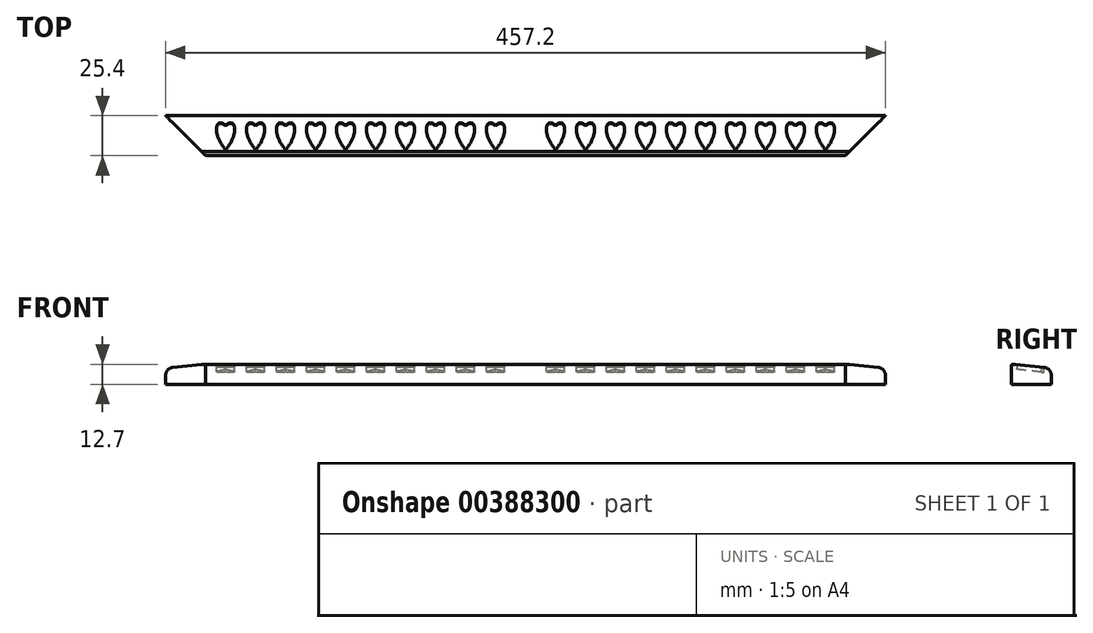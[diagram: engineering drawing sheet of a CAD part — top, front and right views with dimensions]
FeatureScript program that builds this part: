
annotation { "Feature Type Name" : "Feature", "Feature Type Description" : "" }
export const myFeature = defineFeature(function(context is Context, id is Id, definition is map)
    precondition{}
    {
        {
            var Q0;
            Q0=qCreatedBy(makeId("Top.planeOp"),FACE);
            var sketch = newSketch(context, id + "F0", { "sketchPlane" : qUnion([Q0])});
            skLineSegment(sketch, "E0.bottom", {"start": v(-228.6, 12.7) * mm, "end": v(228.6, 12.7) * mm});
            skLineSegment(sketch, "E0.top", {"start": v(-228.6, -12.7) * mm, "end": v(228.6, -12.7) * mm});
            skLineSegment(sketch, "E0.left", {"start": v(-228.6, 12.7) * mm, "end": v(-228.6, -12.7) * mm});
            skLineSegment(sketch, "E0.right", {"start": v(228.6, 12.7) * mm, "end": v(228.6, -12.7) * mm});
            skPoint(sketch, "E0.middle", {"position": v(0, 0) * mm});
            skLineSegment(sketch, "E1", {"start": v(-228.6, 12.7) * mm, "end": v(-203.2, -12.7) * mm});
            skLineSegment(sketch, "E2.MirrorCS", {"start": v(228.6, 12.7) * mm, "end": v(203.2, -12.7) * mm});
            skSolve(sketch);
        }
        {
            var Q0;
            Q0=makeQuery(id+"F0.imprint","IMPRINT",FACE,{"disambiguationData":[TD([[makeQuery(id+"F0.imprint","IMPRINT",EDGE,{"derivedFrom":sQuery(id+"F0.wireOp",EDGE,"E0.bottom")}),-1.0]])]});
            extrude(context, id + "F1", {"entities" : qUnion([Q0]), "depth" : 12.7 * mm});
        }
        {
            var Q0;
            Q0=makeQuery(id+"F1.opExtrude","CAP_EDGE",EDGE,{"disambiguationData":[OSD([sQuery(id+"F0.wireOp",EDGE,"E0.bottom")])],"isStart":false});
            chamfer(context, id + "F2", {"entities" : qUnion([Q0]), "chamferType" : ChamferType.TWO_OFFSETS, "width1" : 2.54 * mm, "oppositeDirection" : false, "width2" : 22.86 * mm, "tangentPropagation" : true});
        }
        {
            var Q0;
            {var subQ0=sQuery(id+"F0.wireOp",EDGE,"E0.bottom");Q0=makeQuery(id+"F2.opChamfer","BLEND_EDGE",EDGE,{"blendedFrom":[makeQuery(id+"F1.opExtrude","CAP_EDGE",EDGE,{"disambiguationData":[OSD([subQ0])],"isStart":false}),makeQuery(id+"F1.opExtrude","SWEPT_FACE",FACE,{"disambiguationData":[OSD([subQ0])]})],"blendedInto":[makeQuery(id+"F1.opExtrude","SWEPT_FACE",FACE,{"disambiguationData":[OSD([subQ0])]})]});}
            fillet(context, id + "F3", {"entities" : qUnion([Q0]), "radius" : 5.08 * mm, "tangentPropagation" : true, "allowEdgeOverflow" : false});
        }
        {
            var Q0;
            Q0=makeQuery(id+"F2.opChamfer","BLEND_FACE",FACE,{"disambiguationData":[OSD([sQuery(id+"F0.wireOp",EDGE,"E0.bottom")])]});
            var sketch = newSketch(context, id + "F4", { "sketchPlane" : qUnion([Q0])});
            skLineSegment(sketch, "E3.bottom", {"start": v(-6.1, 6.86) * mm, "end": v(6.1, 6.86) * mm});
            skLineSegment(sketch, "E3.top", {"start": v(-6.1, -11.6) * mm, "end": v(6.1, -11.6) * mm});
            skLineSegment(sketch, "E3.left", {"start": v(-6.1, 6.86) * mm, "end": v(-6.1, -11.6) * mm});
            skLineSegment(sketch, "E3.right", {"start": v(6.1, 6.86) * mm, "end": v(6.1, -11.6) * mm});
            skPoint(sketch, "E3.middle", {"position": v(0, -2.36) * mm});
            skPoint(sketch, "E3.middle.positionSnap0", {"position": v(-189.51, -2.36) * mm});
            skPoint(sketch, "E3.centerSnap0", {"position": v(-189.51, -2.36) * mm});
            skEllipticalArc(sketch, "E4", {});
            skEllipticalArc(sketch, "E5", {});
            skEllipticalArc(sketch, "E6.0.1.0", {});
            skEllipticalArc(sketch, "E6.0.1.1", {});
            skEllipticalArc(sketch, "E6.1.0.0", {});
            skEllipticalArc(sketch, "E6.1.0.1", {});
            skEllipticalArc(sketch, "E6.1.1.0", {});
            skEllipticalArc(sketch, "E6.1.1.1", {});
            skEllipticalArc(sketch, "E6.2.0.0", {});
            skEllipticalArc(sketch, "E6.2.0.1", {});
            skEllipticalArc(sketch, "E6.2.1.0", {});
            skEllipticalArc(sketch, "E6.2.1.1", {});
            skEllipticalArc(sketch, "E6.3.0.0", {});
            skEllipticalArc(sketch, "E6.3.0.1", {});
            skEllipticalArc(sketch, "E6.3.1.0", {});
            skEllipticalArc(sketch, "E6.3.1.1", {});
            skEllipticalArc(sketch, "E6.4.0.0", {});
            skEllipticalArc(sketch, "E6.4.0.1", {});
            skEllipticalArc(sketch, "E6.4.1.0", {});
            skEllipticalArc(sketch, "E6.4.1.1", {});
            skEllipticalArc(sketch, "E6.5.0.0", {});
            skEllipticalArc(sketch, "E6.5.0.1", {});
            skEllipticalArc(sketch, "E6.5.1.0", {});
            skEllipticalArc(sketch, "E6.5.1.1", {});
            skEllipticalArc(sketch, "E6.6.0.0", {});
            skEllipticalArc(sketch, "E6.6.0.1", {});
            skEllipticalArc(sketch, "E6.6.1.0", {});
            skEllipticalArc(sketch, "E6.6.1.1", {});
            skEllipticalArc(sketch, "E6.7.0.0", {});
            skEllipticalArc(sketch, "E6.7.0.1", {});
            skEllipticalArc(sketch, "E6.7.1.0", {});
            skEllipticalArc(sketch, "E6.7.1.1", {});
            skEllipticalArc(sketch, "E6.8.0.0", {});
            skEllipticalArc(sketch, "E6.8.0.1", {});
            skEllipticalArc(sketch, "E6.8.1.0", {});
            skEllipticalArc(sketch, "E6.8.1.1", {});
            skEllipticalArc(sketch, "E6.9.0.0", {});
            skEllipticalArc(sketch, "E6.9.0.1", {});
            skEllipticalArc(sketch, "E6.9.1.0", {});
            skEllipticalArc(sketch, "E6.9.1.1", {});
            skLineSegment(sketch, "E6.direction1", {"start": v(0, -10.06) * mm, "end": v(19.05, -10.06) * mm, "construction": true});
            skLineSegment(sketch, "E6.direction2", {"start": v(0, -10.06) * mm, "end": v(-190.5, -10.06) * mm, "construction": true});
            skEllipticalArc(sketch, "E7.0.10.0", {});
            skEllipticalArc(sketch, "E7.4.10.0", {});
            skEllipticalArc(sketch, "E7.0.10.1", {});
            skEllipticalArc(sketch, "E7.4.10.1", {});
            const initialGuessF4  = {"E4": [0, -0.0023644506516210797, 0.41355218363854207, 0.9104804179156154, 0.010033, 0.004445, 3.9394450816196147, 0.7978524280298204], "E5": [0, -0.0023644506516210797, -0.41355218363854224, 0.9104804179156154, 0.010033, 0.004445, 5.485332879149764, 2.3437402255599724], "E6.0.1.0": [-0.1905, -0.0023644506516211005, -0.4135521836385429, 0.9104804179156151, 0.010033, 0.004445, 5.485332879149764, 2.34374022555997], "E6.0.1.1": [-0.1905, -0.0023644506516211005, 0.4135521836385428, 0.9104804179156151, 0.010033, 0.004445, 3.939445081619611, 0.797852428029822], "E6.1.0.0": [0.01905, -0.0023644506516210797, -0.41355218363854224, 0.9104804179156153, 0.010033, 0.004445, 5.485332879149765, 2.3437402255599733], "E6.1.0.1": [0.01905, -0.0023644506516210797, 0.41355218363854207, 0.9104804179156155, 0.010033, 0.004445, 3.939445081619616, 0.7978524280298207], "E6.1.1.0": [-0.17145, -0.0023644506516211005, -0.41355218363854285, 0.9104804179156151, 0.010033, 0.004445, 5.485332879149765, 2.343740225559971], "E6.1.1.1": [-0.17145, -0.0023644506516211005, 0.4135521836385428, 0.9104804179156152, 0.010033, 0.004445, 3.9394450816196143, 0.7978524280298254], "E6.2.0.0": [0.0381, -0.0023644506516210797, -0.41355218363854224, 0.9104804179156153, 0.010033, 0.004445, 5.485332879149765, 2.3437402255599724], "E6.2.0.1": [0.0381, -0.0023644506516210797, 0.41355218363854207, 0.9104804179156155, 0.010033, 0.004445, 3.939445081619614, 0.7978524280298207], "E6.2.1.0": [-0.1524, -0.0023644506516211005, -0.41355218363854285, 0.9104804179156151, 0.010033, 0.004445, 5.485332879149764, 2.343740225559971], "E6.2.1.1": [-0.1524, -0.0023644506516211005, 0.4135521836385428, 0.9104804179156152, 0.010033, 0.004445, 3.9394450816196143, 0.7978524280298218], "E6.3.0.0": [0.05715, -0.0023644506516210797, -0.41355218363854224, 0.9104804179156153, 0.010033, 0.004445, 5.485332879149765, 2.3437402255599724], "E6.3.0.1": [0.05715, -0.0023644506516210797, 0.41355218363854207, 0.9104804179156155, 0.010033, 0.004445, 3.939445081619614, 0.7978524280298207], "E6.3.1.0": [-0.13335, -0.0023644506516211005, -0.41355218363854285, 0.9104804179156151, 0.010033, 0.004445, 5.485332879149764, 2.343740225559971], "E6.3.1.1": [-0.13335, -0.0023644506516211005, 0.4135521836385428, 0.9104804179156152, 0.010033, 0.004445, 3.9394450816196143, 0.7978524280298218], "E6.4.0.0": [0.0762, -0.0023644506516210797, -0.41355218363854224, 0.9104804179156153, 0.010033, 0.004445, 5.485332879149765, 2.3437402255599724], "E6.4.0.1": [0.0762, -0.0023644506516210797, 0.41355218363854207, 0.9104804179156155, 0.010033, 0.004445, 3.939445081619614, 0.7978524280298207], "E6.4.1.0": [-0.1143, -0.0023644506516211005, -0.41355218363854285, 0.9104804179156151, 0.010033, 0.004445, 5.485332879149764, 2.343740225559971], "E6.4.1.1": [-0.1143, -0.0023644506516211005, 0.4135521836385428, 0.9104804179156152, 0.010033, 0.004445, 3.9394450816196143, 0.7978524280298218], "E6.5.0.0": [0.09525, -0.0023644506516210797, -0.41355218363854224, 0.9104804179156153, 0.010033, 0.004445, 5.485332879149765, 2.3437402255599724], "E6.5.0.1": [0.09525, -0.0023644506516210797, 0.41355218363854207, 0.9104804179156155, 0.010033, 0.004445, 3.939445081619614, 0.7978524280298207], "E6.5.1.0": [-0.09525, -0.0023644506516211005, -0.41355218363854285, 0.9104804179156151, 0.010033, 0.004445, 5.485332879149764, 2.343740225559971], "E6.5.1.1": [-0.09525, -0.0023644506516211005, 0.4135521836385428, 0.9104804179156152, 0.010033, 0.004445, 3.9394450816196143, 0.7978524280298218], "E6.6.0.0": [0.1143, -0.0023644506516210797, -0.41355218363854224, 0.9104804179156153, 0.010033, 0.004445, 5.485332879149765, 2.3437402255599724], "E6.6.0.1": [0.1143, -0.0023644506516210797, 0.41355218363854207, 0.9104804179156155, 0.010033, 0.004445, 3.939445081619614, 0.7978524280298207], "E6.6.1.0": [-0.0762, -0.0023644506516211005, -0.41355218363854285, 0.9104804179156151, 0.010033, 0.004445, 5.485332879149764, 2.343740225559971], "E6.6.1.1": [-0.0762, -0.0023644506516211005, 0.4135521836385428, 0.9104804179156152, 0.010033, 0.004445, 3.9394450816196143, 0.7978524280298218], "E6.7.0.0": [0.13335, -0.0023644506516210797, -0.41355218363854224, 0.9104804179156153, 0.010033, 0.004445, 5.485332879149765, 2.3437402255599724], "E6.7.0.1": [0.13335, -0.0023644506516210797, 0.41355218363854207, 0.9104804179156155, 0.010033, 0.004445, 3.939445081619614, 0.7978524280298207], "E6.7.1.0": [-0.05715, -0.0023644506516211005, -0.41355218363854285, 0.9104804179156151, 0.010033, 0.004445, 5.485332879149764, 2.343740225559971], "E6.7.1.1": [-0.05715, -0.0023644506516211005, 0.4135521836385428, 0.9104804179156152, 0.010033, 0.004445, 3.9394450816196143, 0.7978524280298218], "E6.8.0.0": [0.1524, -0.0023644506516210797, -0.41355218363854224, 0.9104804179156153, 0.010033, 0.004445, 5.485332879149765, 2.3437402255599724], "E6.8.0.1": [0.1524, -0.0023644506516210797, 0.41355218363854207, 0.9104804179156155, 0.010033, 0.004445, 3.939445081619614, 0.7978524280298207], "E6.8.1.0": [-0.0381, -0.0023644506516211005, -0.41355218363854285, 0.9104804179156151, 0.010033, 0.004445, 5.485332879149764, 2.343740225559971], "E6.8.1.1": [-0.0381, -0.0023644506516211005, 0.4135521836385428, 0.9104804179156152, 0.010033, 0.004445, 3.9394450816196143, 0.7978524280298218], "E6.9.0.0": [0.17145, -0.0023644506516210797, -0.41355218363854224, 0.9104804179156153, 0.010033, 0.004445, 5.485332879149765, 2.3437402255599724], "E6.9.0.1": [0.17145, -0.0023644506516210797, 0.41355218363854207, 0.9104804179156155, 0.010033, 0.004445, 3.939445081619614, 0.7978524280298207], "E6.9.1.0": [-0.01905, -0.0023644506516211005, -0.41355218363854285, 0.9104804179156151, 0.010033, 0.004445, 5.485332879149764, 2.3437402255599715], "E6.9.1.1": [-0.01905, -0.0023644506516211005, 0.4135521836385428, 0.9104804179156152, 0.010033, 0.004445, 3.9394450816196147, 0.7978524280298215], "E7.0.10.0": [0.1905, -0.0023644506516210797, -0.41355218363854224, 0.9104804179156154, 0.010033, 0.004445, 5.485332879149765, 2.3437402255599724], "E7.4.10.0": [0.1905, -0.0023644506516210797, 0.41355218363854207, 0.9104804179156154, 0.010033, 0.004445, 3.939445081619614, 0.7978524280298207], "E7.0.10.1": [0, -0.0023644506516211005, -0.4135521836385429, 0.9104804179156151, 0.010033, 0.004445, 5.485332879149764, 2.3437402255599706], "E7.4.10.1": [0, -0.0023644506516211005, 0.4135521836385428, 0.9104804179156151, 0.010033, 0.004445, 3.9394450816196143, 0.7978524280298223]};
            skSetInitialGuess(sketch, initialGuessF4);
            skSolve(sketch);
        }
        {
            var Q0;
            {var subQ0=sQuery(id+"F4.wireOp",EDGE,"E6.0.1.1");var subQ1=sQuery(id+"F4.wireOp",EDGE,"E6.0.1.0");var subQ2=makeQuery(id+"F4.imprint","INTERSECT",VERTEX,{"disambiguationData":[OD(0.0)],"derivedFrom":[subQ1,subQ0]});Q0=makeQuery(id+"F4.imprint","IMPRINT",FACE,{"disambiguationData":[TD([[makeQuery(id+"F4.imprint","IMPRINT",EDGE,{"disambiguationData":[TD([[subQ2,-1.0]])],"derivedFrom":subQ1}),1.0]])]});}
            var Q1;
            {var subQ0=sQuery(id+"F4.wireOp",EDGE,"E6.1.1.1");var subQ1=sQuery(id+"F4.wireOp",EDGE,"E6.1.1.0");var subQ2=makeQuery(id+"F4.imprint","INTERSECT",VERTEX,{"disambiguationData":[OD(0.0)],"derivedFrom":[subQ1,subQ0]});Q1=makeQuery(id+"F4.imprint","IMPRINT",FACE,{"disambiguationData":[TD([[makeQuery(id+"F4.imprint","IMPRINT",EDGE,{"disambiguationData":[TD([[subQ2,-1.0]])],"derivedFrom":subQ1}),1.0]])]});}
            var Q2;
            {var subQ0=sQuery(id+"F4.wireOp",EDGE,"E6.2.1.1");var subQ1=sQuery(id+"F4.wireOp",EDGE,"E6.2.1.0");var subQ2=makeQuery(id+"F4.imprint","INTERSECT",VERTEX,{"disambiguationData":[OD(0.0)],"derivedFrom":[subQ1,subQ0]});Q2=makeQuery(id+"F4.imprint","IMPRINT",FACE,{"disambiguationData":[TD([[makeQuery(id+"F4.imprint","IMPRINT",EDGE,{"disambiguationData":[TD([[subQ2,-1.0]])],"derivedFrom":subQ1}),1.0]])]});}
            var Q3;
            {var subQ0=sQuery(id+"F4.wireOp",EDGE,"E6.3.1.1");var subQ1=sQuery(id+"F4.wireOp",EDGE,"E6.3.1.0");var subQ2=makeQuery(id+"F4.imprint","INTERSECT",VERTEX,{"disambiguationData":[OD(0.0)],"derivedFrom":[subQ1,subQ0]});Q3=makeQuery(id+"F4.imprint","IMPRINT",FACE,{"disambiguationData":[TD([[makeQuery(id+"F4.imprint","IMPRINT",EDGE,{"disambiguationData":[TD([[subQ2,-1.0]])],"derivedFrom":subQ1}),1.0]])]});}
            var Q4;
            {var subQ0=sQuery(id+"F4.wireOp",EDGE,"E6.4.1.1");var subQ1=sQuery(id+"F4.wireOp",EDGE,"E6.4.1.0");var subQ2=makeQuery(id+"F4.imprint","INTERSECT",VERTEX,{"disambiguationData":[OD(0.0)],"derivedFrom":[subQ1,subQ0]});Q4=makeQuery(id+"F4.imprint","IMPRINT",FACE,{"disambiguationData":[TD([[makeQuery(id+"F4.imprint","IMPRINT",EDGE,{"disambiguationData":[TD([[subQ2,-1.0]])],"derivedFrom":subQ1}),1.0]])]});}
            var Q5;
            {var subQ0=sQuery(id+"F4.wireOp",EDGE,"E6.5.1.1");var subQ1=sQuery(id+"F4.wireOp",EDGE,"E6.5.1.0");var subQ2=makeQuery(id+"F4.imprint","INTERSECT",VERTEX,{"disambiguationData":[OD(0.0)],"derivedFrom":[subQ1,subQ0]});Q5=makeQuery(id+"F4.imprint","IMPRINT",FACE,{"disambiguationData":[TD([[makeQuery(id+"F4.imprint","IMPRINT",EDGE,{"disambiguationData":[TD([[subQ2,-1.0]])],"derivedFrom":subQ1}),1.0]])]});}
            var Q6;
            {var subQ0=sQuery(id+"F4.wireOp",EDGE,"E6.6.1.1");var subQ1=sQuery(id+"F4.wireOp",EDGE,"E6.6.1.0");var subQ2=makeQuery(id+"F4.imprint","INTERSECT",VERTEX,{"disambiguationData":[OD(0.0)],"derivedFrom":[subQ1,subQ0]});Q6=makeQuery(id+"F4.imprint","IMPRINT",FACE,{"disambiguationData":[TD([[makeQuery(id+"F4.imprint","IMPRINT",EDGE,{"disambiguationData":[TD([[subQ2,-1.0]])],"derivedFrom":subQ1}),1.0]])]});}
            var Q7;
            {var subQ0=sQuery(id+"F4.wireOp",EDGE,"E6.7.1.1");var subQ1=sQuery(id+"F4.wireOp",EDGE,"E6.7.1.0");var subQ2=makeQuery(id+"F4.imprint","INTERSECT",VERTEX,{"disambiguationData":[OD(0.0)],"derivedFrom":[subQ1,subQ0]});Q7=makeQuery(id+"F4.imprint","IMPRINT",FACE,{"disambiguationData":[TD([[makeQuery(id+"F4.imprint","IMPRINT",EDGE,{"disambiguationData":[TD([[subQ2,-1.0]])],"derivedFrom":subQ1}),1.0]])]});}
            var Q8;
            {var subQ0=sQuery(id+"F4.wireOp",EDGE,"E6.8.1.1");var subQ1=sQuery(id+"F4.wireOp",EDGE,"E6.8.1.0");var subQ2=makeQuery(id+"F4.imprint","INTERSECT",VERTEX,{"disambiguationData":[OD(0.0)],"derivedFrom":[subQ1,subQ0]});Q8=makeQuery(id+"F4.imprint","IMPRINT",FACE,{"disambiguationData":[TD([[makeQuery(id+"F4.imprint","IMPRINT",EDGE,{"disambiguationData":[TD([[subQ2,-1.0]])],"derivedFrom":subQ1}),1.0]])]});}
            var Q9;
            {var subQ1=sQuery(id+"F4.wireOp",EDGE,"E6.9.1.0");var subQ3=sQuery(id+"F4.wireOp",EDGE,"E3.bottom");var subQ4=makeQuery(id+"F4.imprint","INTERSECT",VERTEX,{"disambiguationData":[OD(0.0)],"derivedFrom":[subQ3,subQ1]});Q9=makeQuery(id+"F4.imprint","IMPRINT",FACE,{"disambiguationData":[TD([[makeQuery(id+"F4.imprint","IMPRINT",EDGE,{"disambiguationData":[TD([[subQ4,-1.0]])],"derivedFrom":subQ3}),-1.0]])]});}
            var Q10;
            {var subQ0=sQuery(id+"F4.wireOp",EDGE,"E6.1.0.1");var subQ1=sQuery(id+"F4.wireOp",EDGE,"E6.1.0.0");var subQ2=makeQuery(id+"F4.imprint","INTERSECT",VERTEX,{"disambiguationData":[OD(0.0)],"derivedFrom":[subQ1,subQ0]});Q10=makeQuery(id+"F4.imprint","IMPRINT",FACE,{"disambiguationData":[TD([[makeQuery(id+"F4.imprint","IMPRINT",EDGE,{"disambiguationData":[TD([[subQ2,-1.0]])],"derivedFrom":subQ1}),1.0]])]});}
            var Q11;
            {var subQ0=sQuery(id+"F4.wireOp",EDGE,"E6.2.0.1");var subQ1=sQuery(id+"F4.wireOp",EDGE,"E6.2.0.0");var subQ2=makeQuery(id+"F4.imprint","INTERSECT",VERTEX,{"disambiguationData":[OD(0.0)],"derivedFrom":[subQ1,subQ0]});Q11=makeQuery(id+"F4.imprint","IMPRINT",FACE,{"disambiguationData":[TD([[makeQuery(id+"F4.imprint","IMPRINT",EDGE,{"disambiguationData":[TD([[subQ2,-1.0]])],"derivedFrom":subQ1}),1.0]])]});}
            var Q12;
            {var subQ0=sQuery(id+"F4.wireOp",EDGE,"E6.3.0.1");var subQ1=sQuery(id+"F4.wireOp",EDGE,"E6.3.0.0");var subQ2=makeQuery(id+"F4.imprint","INTERSECT",VERTEX,{"disambiguationData":[OD(0.0)],"derivedFrom":[subQ1,subQ0]});Q12=makeQuery(id+"F4.imprint","IMPRINT",FACE,{"disambiguationData":[TD([[makeQuery(id+"F4.imprint","IMPRINT",EDGE,{"disambiguationData":[TD([[subQ2,-1.0]])],"derivedFrom":subQ1}),1.0]])]});}
            var Q13;
            {var subQ0=sQuery(id+"F4.wireOp",EDGE,"E6.9.0.1");var subQ1=sQuery(id+"F4.wireOp",EDGE,"E6.9.0.0");var subQ2=makeQuery(id+"F4.imprint","INTERSECT",VERTEX,{"disambiguationData":[OD(0.0)],"derivedFrom":[subQ1,subQ0]});Q13=makeQuery(id+"F4.imprint","IMPRINT",FACE,{"disambiguationData":[TD([[makeQuery(id+"F4.imprint","IMPRINT",EDGE,{"disambiguationData":[TD([[subQ2,-1.0]])],"derivedFrom":subQ1}),1.0]])]});}
            var Q14;
            {var subQ0=sQuery(id+"F4.wireOp",EDGE,"E6.8.0.1");var subQ1=sQuery(id+"F4.wireOp",EDGE,"E6.8.0.0");var subQ2=makeQuery(id+"F4.imprint","INTERSECT",VERTEX,{"disambiguationData":[OD(0.0)],"derivedFrom":[subQ1,subQ0]});Q14=makeQuery(id+"F4.imprint","IMPRINT",FACE,{"disambiguationData":[TD([[makeQuery(id+"F4.imprint","IMPRINT",EDGE,{"disambiguationData":[TD([[subQ2,-1.0]])],"derivedFrom":subQ1}),1.0]])]});}
            var Q15;
            {var subQ0=sQuery(id+"F4.wireOp",EDGE,"E6.7.0.1");var subQ1=sQuery(id+"F4.wireOp",EDGE,"E6.7.0.0");var subQ2=makeQuery(id+"F4.imprint","INTERSECT",VERTEX,{"disambiguationData":[OD(0.0)],"derivedFrom":[subQ1,subQ0]});Q15=makeQuery(id+"F4.imprint","IMPRINT",FACE,{"disambiguationData":[TD([[makeQuery(id+"F4.imprint","IMPRINT",EDGE,{"disambiguationData":[TD([[subQ2,-1.0]])],"derivedFrom":subQ1}),1.0]])]});}
            var Q16;
            {var subQ0=sQuery(id+"F4.wireOp",EDGE,"E6.6.0.1");var subQ1=sQuery(id+"F4.wireOp",EDGE,"E6.6.0.0");var subQ2=makeQuery(id+"F4.imprint","INTERSECT",VERTEX,{"disambiguationData":[OD(0.0)],"derivedFrom":[subQ1,subQ0]});Q16=makeQuery(id+"F4.imprint","IMPRINT",FACE,{"disambiguationData":[TD([[makeQuery(id+"F4.imprint","IMPRINT",EDGE,{"disambiguationData":[TD([[subQ2,-1.0]])],"derivedFrom":subQ1}),1.0]])]});}
            var Q17;
            {var subQ0=sQuery(id+"F4.wireOp",EDGE,"E6.5.0.1");var subQ1=sQuery(id+"F4.wireOp",EDGE,"E6.5.0.0");var subQ2=makeQuery(id+"F4.imprint","INTERSECT",VERTEX,{"disambiguationData":[OD(0.0)],"derivedFrom":[subQ1,subQ0]});Q17=makeQuery(id+"F4.imprint","IMPRINT",FACE,{"disambiguationData":[TD([[makeQuery(id+"F4.imprint","IMPRINT",EDGE,{"disambiguationData":[TD([[subQ2,-1.0]])],"derivedFrom":subQ1}),1.0]])]});}
            var Q18;
            {var subQ0=sQuery(id+"F4.wireOp",EDGE,"E6.4.0.1");var subQ1=sQuery(id+"F4.wireOp",EDGE,"E6.4.0.0");var subQ2=makeQuery(id+"F4.imprint","INTERSECT",VERTEX,{"disambiguationData":[OD(0.0)],"derivedFrom":[subQ1,subQ0]});Q18=makeQuery(id+"F4.imprint","IMPRINT",FACE,{"disambiguationData":[TD([[makeQuery(id+"F4.imprint","IMPRINT",EDGE,{"disambiguationData":[TD([[subQ2,-1.0]])],"derivedFrom":subQ1}),1.0]])]});}
            var Q19;
            {var subQ1=sQuery(id+"F4.wireOp",EDGE,"E7.0.10.1");var subQ3=sQuery(id+"F4.wireOp",EDGE,"E3.bottom");var subQ6=makeQuery(id+"F4.imprint","INTERSECT",VERTEX,{"disambiguationData":[OD(0.0)],"derivedFrom":[subQ3,subQ1]});Q19=makeQuery(id+"F4.imprint","IMPRINT",FACE,{"disambiguationData":[TD([[makeQuery(id+"F4.imprint","IMPRINT",EDGE,{"disambiguationData":[TD([[subQ6,-1.0]])],"derivedFrom":subQ3}),-1.0]])]});}
            var Q20;
            {var subQ0=sQuery(id+"F4.wireOp",EDGE,"E6.9.1.1");var subQ1=sQuery(id+"F4.wireOp",EDGE,"E6.9.1.0");var subQ2=makeQuery(id+"F4.imprint","INTERSECT",VERTEX,{"disambiguationData":[OD(0.0)],"derivedFrom":[subQ1,subQ0]});Q20=makeQuery(id+"F4.imprint","IMPRINT",FACE,{"disambiguationData":[TD([[makeQuery(id+"F4.imprint","IMPRINT",EDGE,{"disambiguationData":[TD([[subQ2,-1.0]])],"derivedFrom":subQ1}),1.0]])]});}
            var Q21;
            {var subQ0=sQuery(id+"F4.wireOp",EDGE,"E7.4.10.0");var subQ1=sQuery(id+"F4.wireOp",EDGE,"E7.0.10.0");var subQ2=makeQuery(id+"F4.imprint","INTERSECT",VERTEX,{"disambiguationData":[OD(0.0)],"derivedFrom":[subQ1,subQ0]});Q21=makeQuery(id+"F4.imprint","IMPRINT",FACE,{"disambiguationData":[TD([[makeQuery(id+"F4.imprint","IMPRINT",EDGE,{"disambiguationData":[TD([[subQ2,-1.0]])],"derivedFrom":subQ1}),1.0]])]});}
            extrude(context, id + "F5", {"entities" : qUnion([Q0, Q1, Q2, Q3, Q4, Q5, Q6, Q7, Q8, Q9, Q10, Q11, Q12, Q13, Q14, Q15, Q16, Q17, Q18, Q19, Q20, Q21]), "operationType" : NewBodyOperationType.REMOVE, "oppositeDirection" : true, "depth" : 3.17 * mm});
        }
    });
